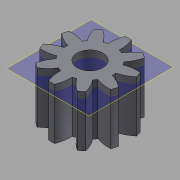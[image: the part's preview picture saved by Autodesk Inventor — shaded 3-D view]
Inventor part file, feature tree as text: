
AUTODESK INVENTOR PART (.ipt)
format: ipt  version: 2015 (Build 190159000, 159)  size: 166,912 bytes
history: native  units: in
note: dims shown in document units (in); Inventor stores cm internally (conversion verified against a paired STEP export)
features: other x13, sketch x3, plane x2
ambient origin geometry x8: Origin, YZ Plane, XZ Plane, XY Plane, X Axis, Y Axis, Z Axis, Center Point
bodies: Solid1 (feature_tree)
feature tree (18):
  other  "Spur Gear18_MIR1.ipt"
  other  "Solid1::Spur Gear18_MIR1.ipt"
  other  "TaggingFeature1"
  sketch  "Sketch1"  dims[d0=0.3937in]
  sketch  "Sketch2"  dims[d16=0.4528in d17=0.0in d41=0.0in d43=0.4528in d46=0.4528in d47=0.0in d48=0.0in]
  sketch  "Sketch3"
  plane  "XZ Plane_1"
  plane  "Work Plane2"
  other  "Z Axis_1"
  other  "Srf1"
  other  "Srf1::Derived"
  other  "Distance iMate"
  other  "Align iMate"
  other  "Mesh iMate"
  other  "Axis iMate"
  other  "Position iMate"
  other  "Mesh iMate2"
  other  "Start plane iMate"
